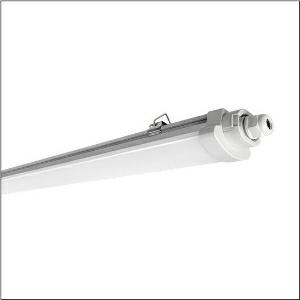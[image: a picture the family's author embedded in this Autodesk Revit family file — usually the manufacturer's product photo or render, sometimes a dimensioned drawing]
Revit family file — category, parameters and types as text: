
# Revit family: monsun_41_51fk20mk440a
name_source: partatom
category: Lighting Fixtures
units: mm (PartAtom-declared; Revit-internal decimal feet)

## family parameters
Cut with Voids When Loaded = No
Host = Face
Light Source = No
Part Type = Normal
Room Calculation Point = No
Round Connector Dimension = Use Diameter
Shared = No

## types (1)
- --- (1 x LED, 4000 lm, 30 W, 4000K)
    Apparent Load = 30 VA
    CIE Flux Codes = 44 74 92 92 100
    Color Rendering = 80
    Color Temperature = 4000K
    Default Elevation = 1800 mm
    Description = Monsun 41, damp-proof luminaire, primary optical cover: diffuser, of PC, frosted, light emission: direct distribution, primary light characteristic: symmetric, installation type: surface-mounted, suspended mounting, LED, rated luminous flux: 4.000lm, luminous efficacy: 130lm/W, light colour: 840, colour temperature: 4000K, control gear: ON/OFF Multilumen, with terminal, 3-pole, mains connection: 220..240V, AC, 50/60Hz, rated input power: 30W, housing, luminaire housing, of PC, grey, length: 1.200mm, width: 79mm, height: 52mm, end cap, of PC, grey, ceiling mounting element, of stainless steel (V2A), protection rating (complete): IP65, insulation class (complete): insulation class II (safety insulation), certification: CE, UKCA, protection symbol: D, impact resistance: IK08, permissible operating ambient temperature: -20..+35°C, corresponds to IFS (International Featured Standards) requirements for safety and quality in the food industry, contact your sales advisor before using the luminaires in applications with unclear chemical exposure, large temperature fluctuations or condensation-forming humidity, packaging unit: 1 piece
    Height = 54 mm
    Lamp = 1 x LED
    Lamp Light Flux = 4000 lm
    Lamp Power = 30 W
    Lamp count = 1
    Length = 1200 mm
    Luminous efficacy = 133 lm/W
    Manufacturer = Siteco
    ModVariant = No
    Model = 51FK20MK440A
    Mounting Place = Ceiling
    Mounting Type = Surface mounted
    Number of Poles = 1
    OnlyDefault = Yes
    Power Factor = 1
    Product Name = Monsun 41
    Product group = damp-proof luminaire
    ProductGroupID = 300
    Protection Class = Protection class II
    Protection Degree = IP 65
    RLX_Detail_Level = 1
    RLX_Emergency_Light_Flux = 0 lm
    RLX_Emergency_Type = 0
    RLX_Emergency_Type_DB = No
    RlxData = <blob elided: 31813 chars, md5=4c4c678c>
    Socket = socket
    Standby Power = 0 W
    System Light Flux = 4000 lm
    System Power = 30 W
    Type Comments = factory setting: luminous flux: 100 % | (HIGH)
    Type Image = l_1007037.jpg
    URL = http://relux.com
    VarID = @adj_174187
    Voltage = 0 V
    Weight = 0.00 kg
    Width = 79 mm

## geometry (parser evidence)
native form markers: Blend x4, Sweep x14
no freeform markers — native parametric forms only
